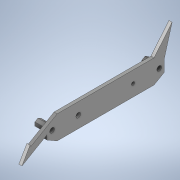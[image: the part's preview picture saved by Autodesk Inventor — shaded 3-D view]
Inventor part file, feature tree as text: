
AUTODESK INVENTOR PART (.ipt)
format: ipt  version: 2020 (Build 240168000, 168)  size: 174,080 bytes
history: native  units: in
note: dims shown in document units (in); Inventor stores cm internally (conversion verified against a paired STEP export)
features: other x3, extrude x2, sketch x2
ambient origin geometry x8: Origin, YZ Plane, XZ Plane, XY Plane, X Axis, Y Axis, Z Axis, Center Point
bodies: Solid1 (feature_tree)
feature tree (7):
  other  "HexWheelGuard.ipt"
  extrude  "Extrusion1"  Depth=0.315in
  extrude  "Extrusion2"  Depth=0.3937in
  other  "Solid1::HexWheelGuard.ipt"
  other  "TaggingFeature2"
  sketch  "Sketch1"  dims[d1=0.3937in d2=0.315in]
  sketch  "Sketch2"  dims[d3=60.0deg d4=1.3858in d5=0.0787in d6=0.3937in d7=0.0in d10=0.3937in d11=1.1024in d12=0.3937in d13=0.0in]
